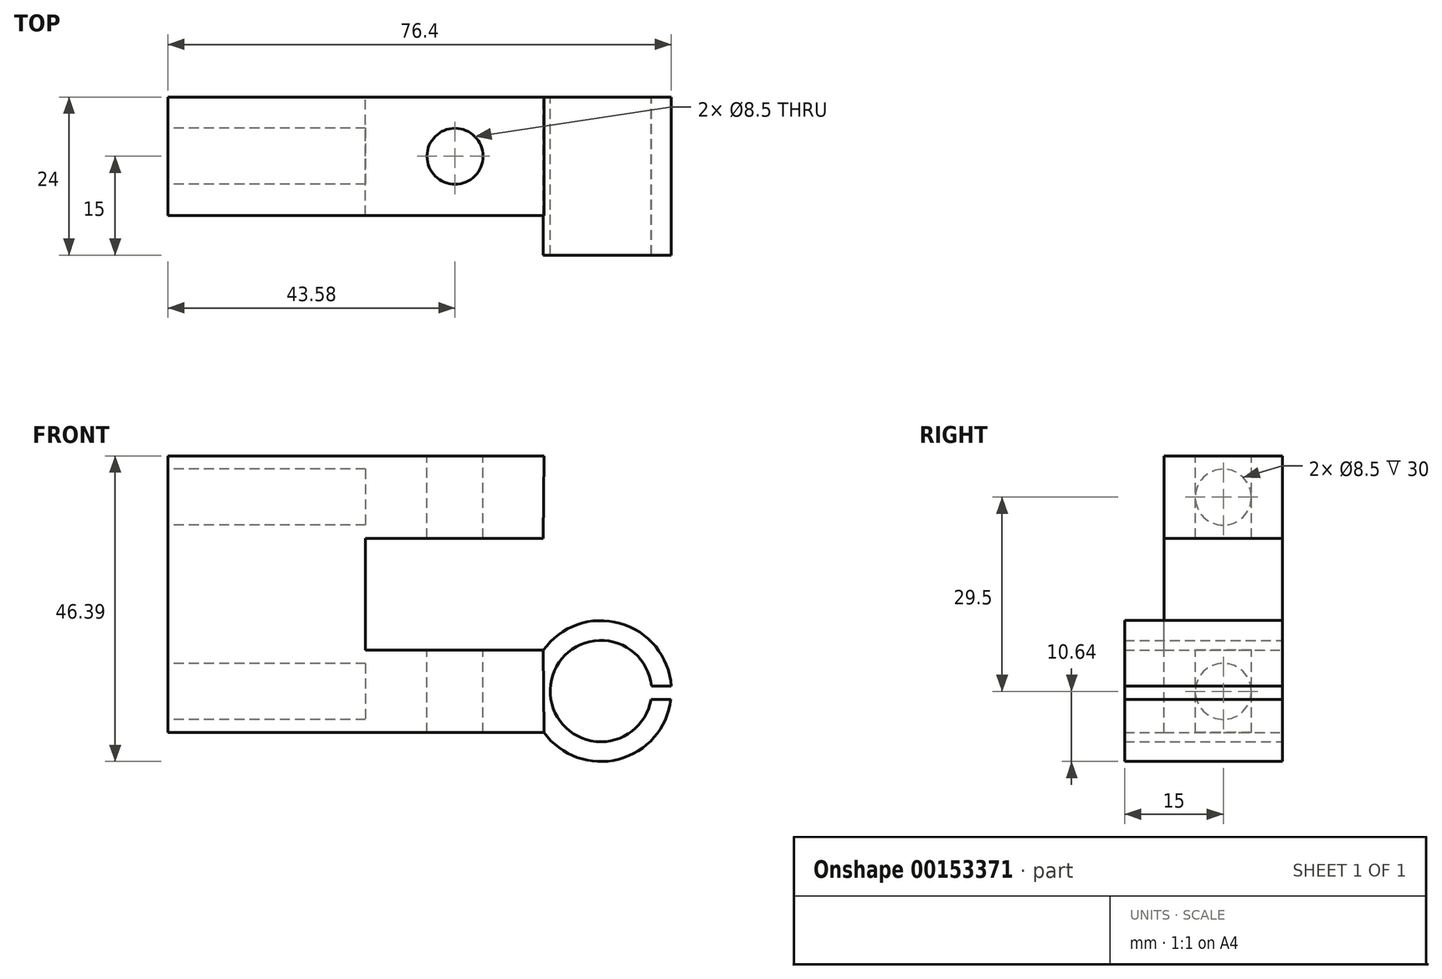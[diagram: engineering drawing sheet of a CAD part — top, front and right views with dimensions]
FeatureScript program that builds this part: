
annotation { "Feature Type Name" : "Feature", "Feature Type Description" : "" }
export const myFeature = defineFeature(function(context is Context, id is Id, definition is map)
    precondition{}
    {
        {
            assignVariable(context, id + "F0", {"name" : "LMXUU_L", "anyValue" : 24});
        }
        {
            assignVariable(context, id + "F1", {"name" : "ZZ", "anyValue" : 22});
        }
        {
            var Q0;
            Q0=qCreatedBy(makeId("Front.planeOp"),FACE);
            var sketch = newSketch(context, id + "F2", { "sketchPlane" : qUnion([Q0])});
            skLineSegment(sketch, "E0.bottom", {"start": v(0, 0) * mm, "end": v(-57.08, 0) * mm});
            skLineSegment(sketch, "E0.top", {"start": v(0, 42) * mm, "end": v(-57.08, 42) * mm});
            skLineSegment(sketch, "E0.right", {"start": v(-57.08, 0) * mm, "end": v(-57.08, 42) * mm});
            skLineSegment(sketch, "E1.bottom", {"start": v(-0.08, 12.5) * mm, "end": v(-27.08, 12.5) * mm});
            skLineSegment(sketch, "E1.top", {"start": v(-0.08, 29.5) * mm, "end": v(-27.08, 29.5) * mm});
            skLineSegment(sketch, "E1.right", {"start": v(-27.08, 12.5) * mm, "end": v(-27.08, 29.5) * mm});
            skLineSegment(sketch, "E2", {"start": v(0, 0) * mm, "end": v(-0.08, 12.5) * mm});
            skLineSegment(sketch, "E3", {"start": v(-0.08, 29.5) * mm, "end": v(0, 42) * mm});
            skCircle(sketch, "E4", {"center": v(8.64, 6.3) * mm, "radius": 7.7 * mm});
            skCircle(sketch, "E5", {"center": v(8.64, 6.3) * mm, "radius": 10.7 * mm});
            skLineSegment(sketch, "E6", {"start": v(-27.08, 21) * mm, "end": v(-27.08, 21.5) * mm});
            skLineSegment(sketch, "E7.bottom", {"start": v(-27.08, 21.5) * mm, "end": v(-0.08, 21.5) * mm});
            skLineSegment(sketch, "E7.top", {"start": v(-27.08, 20.5) * mm, "end": v(-0.08, 20.5) * mm});
            skLineSegment(sketch, "E7.right", {"start": v(-0.08, 21.5) * mm, "end": v(-0.08, 20.5) * mm});
            skSolve(sketch);
        }
        {
            var Q0;
            {var subQ3=sQuery(id+"F2.wireOp",EDGE,"E0.bottom");Q0=makeQuery(id+"F2.imprint","IMPRINT",FACE,{"disambiguationData":[TD([[makeQuery(id+"F2.imprint","IMPRINT",EDGE,{"derivedFrom":subQ3}),-1.0]])]});}
            var Q1;
            {var subQ0=sQuery(id+"F2.wireOp",EDGE,"E2");Q1=makeQuery(id+"F2.imprint","IMPRINT",FACE,{"disambiguationData":[TD([[makeQuery(id+"F2.imprint","IMPRINT",EDGE,{"derivedFrom":subQ0}),1.0]])]});}
            var Q2;
            {var subQ3=sQuery(id+"F2.wireOp",EDGE,"E0.bottom");Q2=makeQuery(id+"F2.imprint","IMPRINT",FACE,{"disambiguationData":[TD([[makeQuery(id+"F2.imprint","IMPRINT",EDGE,{"derivedFrom":subQ3}),-1.0]])]});}
            var Q3;
            {var subQ1=sQuery(id+"F2.wireOp",EDGE,"E6");Q3=makeQuery(id+"F2.imprint","IMPRINT",FACE,{"disambiguationData":[TD([[makeQuery(id+"F2.imprint","IMPRINT",EDGE,{"derivedFrom":subQ1}),-1.0]])]});}
            extrude(context, id + "F3", {"entities" : qUnion([Q0, Q1, Q2, Q3]), "depth" : (getVariable(context, 'ZZ') - 4) * mm});
        }
        {
            var Q0;
            Q0=makeQuery(id+"F3.opExtrude","SWEPT_FACE",FACE,{"disambiguationData":[OSD([sQuery(id+"F2.wireOp",EDGE,"E0.right")])]});
            var sketch = newSketch(context, id + "F4", { "sketchPlane" : qUnion([Q0])});
            skCircle(sketch, "E8", {"center": v(9, 35.75) * mm, "radius": 4.25 * mm});
            skPoint(sketch, "E8.centerSnap0", {"position": v(9, 42) * mm});
            skCircle(sketch, "E9", {"center": v(9, 6.25) * mm, "radius": 4.25 * mm});
            skPoint(sketch, "E9.centerSnap0", {"position": v(9, 0) * mm});
            skSolve(sketch);
        }
        {
            var Q0;
            Q0=makeQuery(id+"F4.imprint","IMPRINT",FACE,{"disambiguationData":[TD([[makeQuery(id+"F4.imprint","IMPRINT",EDGE,{"derivedFrom":sQuery(id+"F4.wireOp",EDGE,"E9")}),1.0]])]});
            var Q1;
            Q1=makeQuery(id+"F4.imprint","IMPRINT",FACE,{"disambiguationData":[TD([[makeQuery(id+"F4.imprint","IMPRINT",EDGE,{"derivedFrom":sQuery(id+"F4.wireOp",EDGE,"E8")}),1.0]])]});
            extrude(context, id + "F5", {"entities" : qUnion([Q0, Q1]), "operationType" : NewBodyOperationType.REMOVE, "oppositeDirection" : true, "depth" : 30 * mm});
        }
        {
            var Q0;
            Q0=makeQuery(id+"F3.opExtrude","SWEPT_FACE",FACE,{"disambiguationData":[OSD([sQuery(id+"F2.wireOp",EDGE,"E0.top")])]});
            var sketch = newSketch(context, id + "F6", { "sketchPlane" : qUnion([Q0])});
            skCircle(sketch, "E10", {"center": v(-13.5, -9) * mm, "radius": 4.25 * mm});
            skPoint(sketch, "E10.centerSnap0", {"position": v(0, -9) * mm});
            skSolve(sketch);
        }
        {
            var Q0;
            Q0=makeQuery(id+"F6.imprint","IMPRINT",FACE,{"disambiguationData":[TD([[makeQuery(id+"F6.imprint","IMPRINT",EDGE,{"derivedFrom":sQuery(id+"F6.wireOp",EDGE,"E10")}),1.0]])]});
            extrude(context, id + "F7", {"entities" : qUnion([Q0]), "operationType" : NewBodyOperationType.REMOVE, "oppositeDirection" : true, "depth" : 100 * mm});
        }
        {
            var Q0;
            {var subQ0=sQuery(id+"F2.wireOp",EDGE,"E2");Q0=makeQuery(id+"F2.imprint","IMPRINT",FACE,{"disambiguationData":[TD([[makeQuery(id+"F2.imprint","IMPRINT",EDGE,{"derivedFrom":subQ0}),-1.0]])]});}
            extrude(context, id + "F8", {"entities" : qUnion([Q0]), "operationType" : NewBodyOperationType.ADD, "depth" : (getVariable(context, 'LMXUU_L')) * mm});
        }
        {
            var Q0;
            Q0=qCreatedBy(makeId("Front.planeOp"),FACE);
            var sketch = newSketch(context, id + "F9", { "sketchPlane" : qUnion([Q0])});
            skLineSegment(sketch, "E11.bottom", {"start": v(13.9, 7.06) * mm, "end": v(21.9, 7.06) * mm});
            skLineSegment(sketch, "E11.top", {"start": v(13.9, 5.06) * mm, "end": v(21.9, 5.06) * mm});
            skLineSegment(sketch, "E11.left", {"start": v(13.9, 7.06) * mm, "end": v(13.9, 5.06) * mm});
            skLineSegment(sketch, "E11.right", {"start": v(21.9, 7.06) * mm, "end": v(21.9, 5.06) * mm});
            skSolve(sketch);
        }
        {
            var Q0;
            Q0=makeQuery(id+"F9.imprint","IMPRINT",FACE,{"disambiguationData":[TD([[makeQuery(id+"F9.imprint","IMPRINT",EDGE,{"derivedFrom":sQuery(id+"F9.wireOp",EDGE,"E11.bottom")}),-1.0]])]});
            extrude(context, id + "F10", {"entities" : qUnion([Q0]), "operationType" : NewBodyOperationType.REMOVE, "depth" : 40 * mm});
        }
    });
